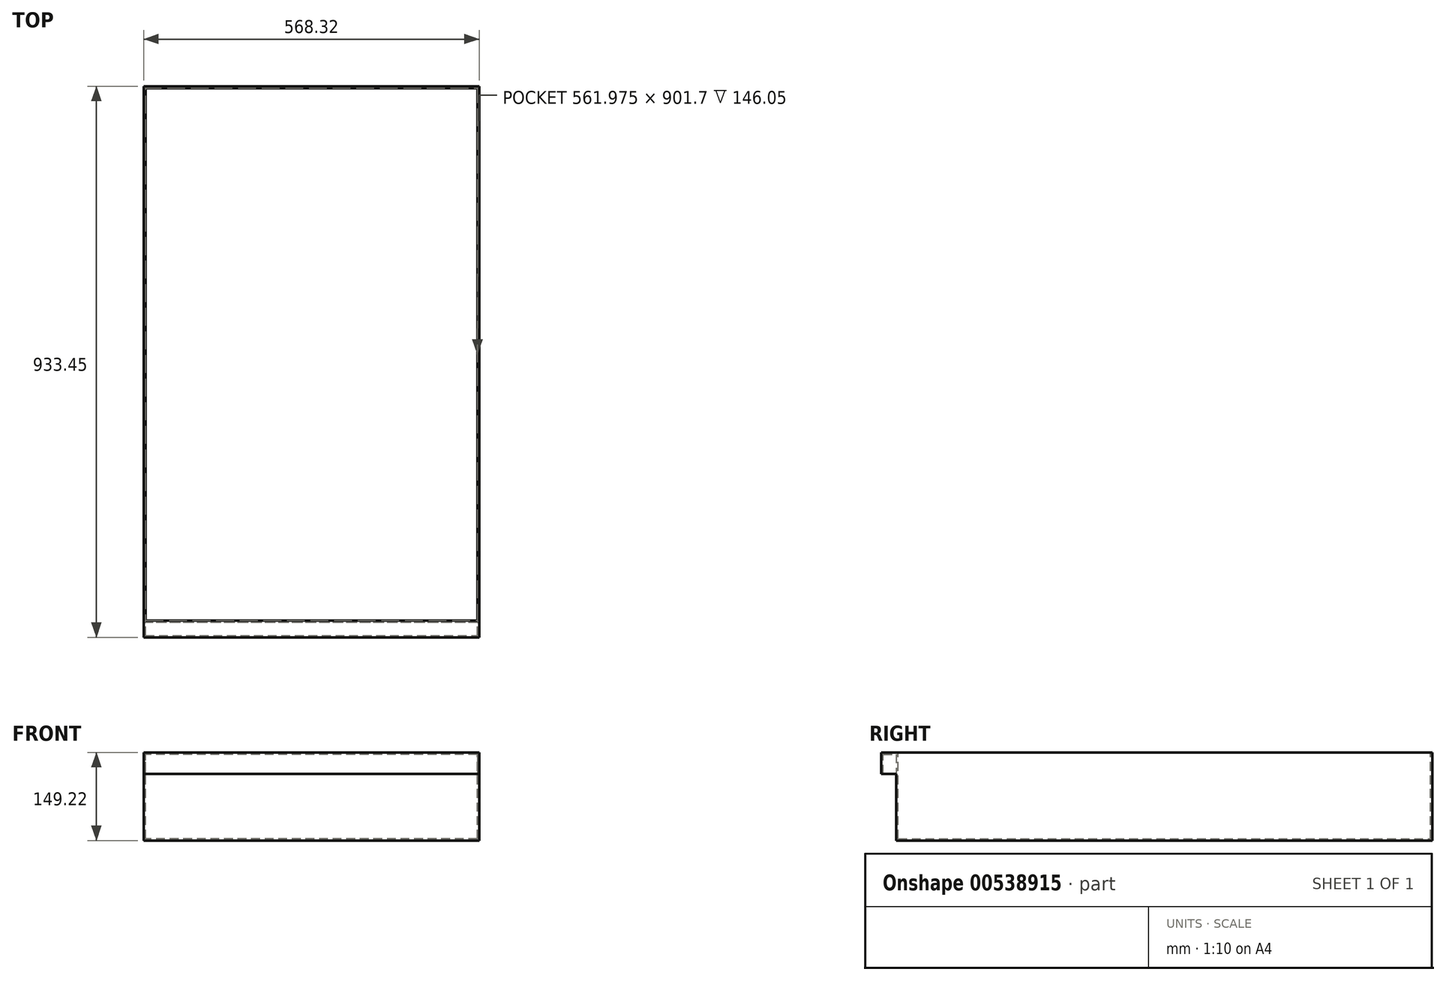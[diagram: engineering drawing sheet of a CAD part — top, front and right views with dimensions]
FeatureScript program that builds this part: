
annotation { "Feature Type Name" : "Feature", "Feature Type Description" : "" }
export const myFeature = defineFeature(function(context is Context, id is Id, definition is map)
    precondition{}
    {
        {
            var Q0;
            Q0=qCreatedBy(makeId("Front.planeOp"),FACE);
            var sketch = newSketch(context, id + "F0", { "sketchPlane" : qUnion([Q0])});
            skLineSegment(sketch, "E0.bottom", {"start": v(284.16, -74.61) * mm, "end": v(-284.16, -74.61) * mm});
            skLineSegment(sketch, "E0.top", {"start": v(284.16, 74.61) * mm, "end": v(-284.16, 74.61) * mm});
            skLineSegment(sketch, "E0.left", {"start": v(284.16, -74.61) * mm, "end": v(284.16, 74.61) * mm});
            skLineSegment(sketch, "E0.right", {"start": v(-284.16, -74.61) * mm, "end": v(-284.16, 74.61) * mm});
            skPoint(sketch, "E0.middle", {"position": v(0, 0) * mm});
            skSolve(sketch);
        }
        {
            var Q0;
            Q0 = qSketchRegion(id + "F0", true);
            extrude(context, id + "F1", {"entities" : qUnion([Q0]), "depth" : 908.05 * mm, "offsetDistance" : 25.4 * mm});
        }
        {
            var Q0;
            Q0=makeQuery(id+"F1.opExtrude","SWEPT_FACE",FACE,{"disambiguationData":[OSD([sQuery(id+"F0.wireOp",EDGE,"E0.top")])]});
            shell(context, id + "F2", {"entities" : qUnion([Q0]), "thickness" : 3.17 * mm});
        }
        {
            var Q0;
            Q0=makeQuery(id+"F1.opExtrude","CAP_FACE",FACE,{"disambiguationData":[OSD([sQuery(id+"F0.wireOp",EDGE,"E0.bottom"),sQuery(id+"F0.wireOp",EDGE,"E0.top"),sQuery(id+"F0.wireOp",EDGE,"E0.left"),sQuery(id+"F0.wireOp",EDGE,"E0.right")])],"isStart":false});
            var sketch = newSketch(context, id + "F3", { "sketchPlane" : qUnion([Q0])});
            skLineSegment(sketch, "E1.bottom", {"start": v(-284.16, 74.61) * mm, "end": v(284.16, 74.61) * mm});
            skLineSegment(sketch, "E1.top", {"start": v(-284.16, 38.14) * mm, "end": v(284.16, 38.14) * mm});
            skLineSegment(sketch, "E1.left", {"start": v(-284.16, 74.61) * mm, "end": v(-284.16, 38.14) * mm});
            skLineSegment(sketch, "E1.right", {"start": v(284.16, 74.61) * mm, "end": v(284.16, 38.14) * mm});
            skSolve(sketch);
        }
        {
            var Q0;
            Q0=makeQuery(id+"F3.imprint","IMPRINT",FACE,{"disambiguationData":[TD([[makeQuery(id+"F3.imprint","IMPRINT",EDGE,{"derivedFrom":sQuery(id+"F3.wireOp",EDGE,"E1.bottom")}),1.0]])]});
            extrude(context, id + "F4", {"entities" : qUnion([Q0]), "operationType" : NewBodyOperationType.ADD, "depth" : 25.4 * mm, "offsetDistance" : 25.4 * mm});
        }
        {
            var Q0;
            Q0=makeQuery(id+"F4.opExtrude","SWEPT_FACE",FACE,{"disambiguationData":[OSD([sQuery(id+"F3.wireOp",EDGE,"E1.top")])]});
            shell(context, id + "F5", {"entities" : qUnion([Q0]), "thickness" : 3.17 * mm});
        }
    });
